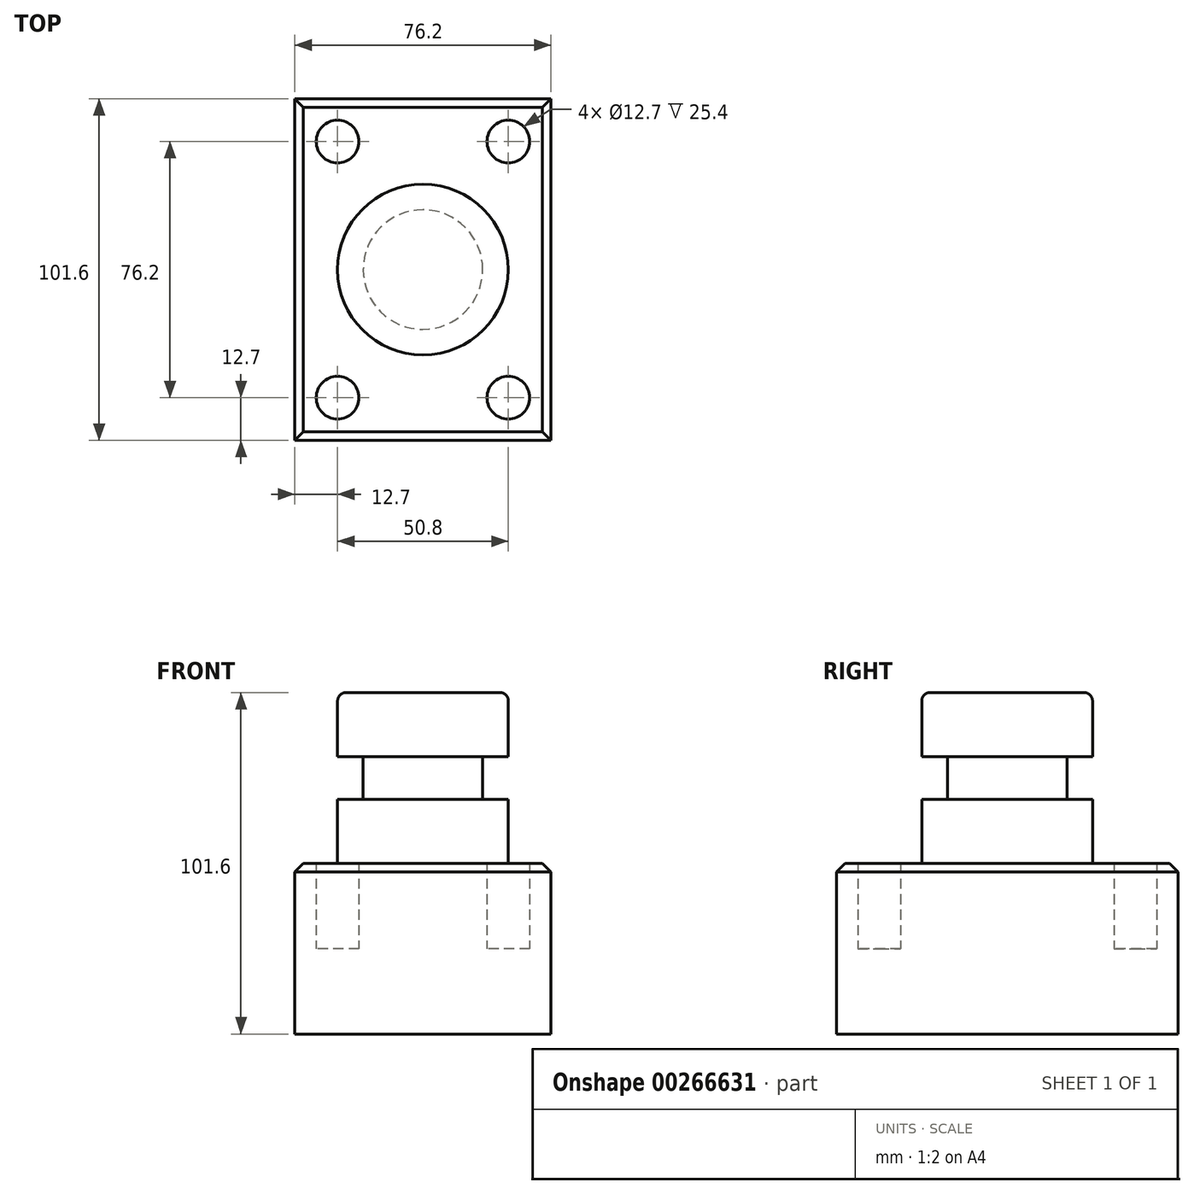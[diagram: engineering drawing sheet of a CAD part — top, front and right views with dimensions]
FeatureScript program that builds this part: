
annotation { "Feature Type Name" : "Feature", "Feature Type Description" : "" }
export const myFeature = defineFeature(function(context is Context, id is Id, definition is map)
    precondition{}
    {
        {
            var Q0;
            Q0=qCreatedBy(makeId("Top.planeOp"),FACE);
            var sketch = newSketch(context, id + "F0", { "sketchPlane" : qUnion([Q0])});
            skLineSegment(sketch, "E0.bottom", {"start": v(-38.1, -50.8) * mm, "end": v(38.1, -50.8) * mm});
            skLineSegment(sketch, "E0.top", {"start": v(-38.1, 50.8) * mm, "end": v(38.1, 50.8) * mm});
            skLineSegment(sketch, "E0.left", {"start": v(-38.1, -50.8) * mm, "end": v(-38.1, 50.8) * mm});
            skLineSegment(sketch, "E0.right", {"start": v(38.1, -50.8) * mm, "end": v(38.1, 50.8) * mm});
            skPoint(sketch, "E0.middle", {"position": v(0, 0) * mm});
            skSolve(sketch);
        }
        {
            var Q0;
            Q0 = qSketchRegion(id + "F0", true);
            extrude(context, id + "F1", {"entities" : qUnion([Q0]), "depth" : 25.4 * mm});
        }
        {
            var Q0;
            Q0=makeQuery(id+"F1.opExtrude","CAP_FACE",FACE,{"disambiguationData":[OSD([sQuery(id+"F0.wireOp",EDGE,"E0.bottom"),sQuery(id+"F0.wireOp",EDGE,"E0.top"),sQuery(id+"F0.wireOp",EDGE,"E0.left"),sQuery(id+"F0.wireOp",EDGE,"E0.right")])],"isStart":false});
            var sketch = newSketch(context, id + "F2", { "sketchPlane" : qUnion([Q0])});
            skCircle(sketch, "E1", {"center": v(-25.4, 38.1) * mm, "radius": 6.35 * mm});
            skCircle(sketch, "E2", {"center": v(25.4, 38.1) * mm, "radius": 6.35 * mm});
            skCircle(sketch, "E3", {"center": v(-25.4, -38.1) * mm, "radius": 6.35 * mm});
            skCircle(sketch, "E4", {"center": v(25.4, -38.1) * mm, "radius": 6.35 * mm});
            skSolve(sketch);
        }
        {
            var Q0;
            Q0=makeQuery(id+"F2.imprint","IMPRINT",FACE,{"disambiguationData":[TD([[makeQuery(id+"F2.imprint","IMPRINT",EDGE,{"derivedFrom":sQuery(id+"F2.wireOp",EDGE,"E1")}),1.0]])]});
            var Q1;
            Q1=makeQuery(id+"F2.imprint","IMPRINT",FACE,{"disambiguationData":[TD([[makeQuery(id+"F2.imprint","IMPRINT",EDGE,{"derivedFrom":sQuery(id+"F2.wireOp",EDGE,"E1")}),-1.0]])]});
            extrude(context, id + "F3", {"entities" : qUnion([Q0, Q1]), "operationType" : NewBodyOperationType.ADD, "depth" : 25.4 * mm});
        }
        {
            var Q0;
            Q0=qCreatedBy(makeId("Front.planeOp"),FACE);
            var sketch = newSketch(context, id + "F4", { "sketchPlane" : qUnion([Q0])});
            skLineSegment(sketch, "E5.bottom", {"start": v(0, 101.6) * mm, "end": v(-25.4, 101.6) * mm});
            skLineSegment(sketch, "E5.top", {"start": v(0, 50.8) * mm, "end": v(-25.4, 50.8) * mm});
            skLineSegment(sketch, "E5.left", {"start": v(0, 101.6) * mm, "end": v(0, 50.8) * mm});
            skLineSegment(sketch, "E5.right", {"start": v(-25.4, 101.6) * mm, "end": v(-25.4, 50.8) * mm});
            skSolve(sketch);
        }
        {
            var Q0;
            Q0=makeQuery(id+"F4.imprint","IMPRINT",FACE,{"disambiguationData":[TD([[makeQuery(id+"F4.imprint","IMPRINT",EDGE,{"derivedFrom":sQuery(id+"F4.wireOp",EDGE,"E5.bottom")}),1.0]])]});
            var Q1;
            Q1=sQuery(id+"F4.wireOp",EDGE,"E5.left");
            revolve(context, id + "F5", {"operationType" : NewBodyOperationType.ADD, "entities" : qUnion([Q0]), "axis" : qUnion([Q1]), "revolveType" : RevolveType.FULL});
        }
        {
            var Q0;
            Q0=qCreatedBy(makeId("Front.planeOp"),FACE);
            var sketch = newSketch(context, id + "F6", { "sketchPlane" : qUnion([Q0])});
            skLineSegment(sketch, "E6.bottom", {"start": v(-36.08, 82.55) * mm, "end": v(-17.78, 82.55) * mm});
            skLineSegment(sketch, "E6.top", {"start": v(-36.08, 69.85) * mm, "end": v(-17.78, 69.85) * mm});
            skLineSegment(sketch, "E6.left", {"start": v(-36.08, 82.55) * mm, "end": v(-36.08, 69.85) * mm});
            skLineSegment(sketch, "E6.right", {"start": v(-17.78, 82.55) * mm, "end": v(-17.78, 69.85) * mm});
            skSolve(sketch);
        }
        {
            var Q0;
            Q0=makeQuery(id+"F6.imprint","IMPRINT",FACE,{"disambiguationData":[TD([[makeQuery(id+"F6.imprint","IMPRINT",EDGE,{"derivedFrom":sQuery(id+"F6.wireOp",EDGE,"E6.bottom")}),-1.0]])]});
            var Q1;
            Q1=makeQuery(id+"F5.opRevolve","SWEPT_EDGE",EDGE,{"disambiguationData":[OSD([sQuery(id+"F4.wireOp",EDGE,"E5.bottom"),sQuery(id+"F4.wireOp",EDGE,"E5.right")])]});
            revolve(context, id + "F7", {"operationType" : NewBodyOperationType.REMOVE, "entities" : qUnion([Q0]), "axis" : qUnion([Q1]), "revolveType" : RevolveType.FULL, "oppositeDirection" : true});
        }
        {
            var Q0;
            Q0=makeQuery(id+"F5.opRevolve","SWEPT_EDGE",EDGE,{"disambiguationData":[OSD([sQuery(id+"F4.wireOp",EDGE,"E5.bottom"),sQuery(id+"F4.wireOp",EDGE,"E5.right")])]});
            var Q1;
            Q1=makeQuery(id+"F5.opRevolve","SWEPT_EDGE",EDGE,{"disambiguationData":[OSD([sQuery(id+"F4.wireOp",EDGE,"E5.top"),sQuery(id+"F4.wireOp",EDGE,"E5.right")])]});
            fillet(context, id + "F8", {"entities" : qUnion([Q0, Q1]), "radius" : 2.54 * mm, "tangentPropagation" : true, "allowEdgeOverflow" : false});
        }
        {
            var Q0;
            Q0=makeQuery(id+"F3.opExtrude","CAP_EDGE",EDGE,{"disambiguationData":[OSD([sQuery(id+"F0.wireOp",EDGE,"E0.bottom")])],"isStart":false});
            var Q1;
            Q1=makeQuery(id+"F3.opExtrude","CAP_EDGE",EDGE,{"disambiguationData":[OSD([sQuery(id+"F0.wireOp",EDGE,"E0.right")])],"isStart":false});
            var Q2;
            Q2=makeQuery(id+"F3.opExtrude","CAP_EDGE",EDGE,{"disambiguationData":[OSD([sQuery(id+"F0.wireOp",EDGE,"E0.top")])],"isStart":false});
            var Q3;
            Q3=makeQuery(id+"F3.opExtrude","CAP_EDGE",EDGE,{"disambiguationData":[OSD([sQuery(id+"F0.wireOp",EDGE,"E0.left")])],"isStart":false});
            chamfer(context, id + "F9", {"entities" : qUnion([Q0, Q1, Q2, Q3]), "width" : 2.54 * mm, "tangentPropagation" : true});
        }
        {
            var Q0;
            Q0 = qSketchRegion(id + "F2", true);
            extrude(context, id + "F10", {"entities" : qUnion([Q0]), "operationType" : NewBodyOperationType.REMOVE, "depth" : 25.4 * mm});
        }
    });
